# Revit family: PRD_FrankeWS_WlMntdFrntrSpprtRls_BagHolderE-RODX605N,E-RODX607
name_source: partatom
category: Furniture
revit_build: Autodesk Revit 2018 (Build: 20190510_1515(x64)
units: mm (PartAtom-declared; Revit-internal decimal feet)

## family parameters
Cut with Voids When Loaded = No
Host = Face
OmniClass Number = 23.40.20.31.11
OmniClass Title = Bins
Room Calculation Point = No
Shared = No

## types (2) — shared parameters
AssetType = Fixed
BagHolderMaterial = PRD_AR_StainlessSteel_SatinFinished
Category = Pr_40_50_07_96, Waste bins
Color = Stainless steel
Default Elevation = 820 mm
DurationUnit = year
Features = stainless steel, 0.80 mm, satin finished
Finish = Satin finished
FinishAndColour = Stainless steel, satin finished
IfcExportAs = IfcFurnitureType
IfcExportType = NOTDEFINED
IntegralAccessories = includes stainless steel screws and nuts
MainColor = Stainless steel
Manufacturer = KWC Group AG
ManufacturerName = KWC Group AG
ManufacturerURL = www.kwc.com
Material = Stainless steel
Materials = Stainless steel 1.4301
NBSDescription = Bag holder
NBSReference = 45-35-35/450
NominalHeight = 61 mm
ProductInformation = https://pim.kwc.com
Style = Bag holder
TypeOfMounting = Bolt mounting
URL = www.kwc.com
Uniclass2015Code = Pr_20_85_07_97
Uniclass2015Title = Bag holder
Uniclass2015Version = Products v1.10
Version = 1
WarrantyDurationUnit = year

## per-type parameters (varying)
| type | BIMObjectName | Description | GrossWeight | ModelNumber | Name | NetWeight | NominalDepth | NominalWidth | OverallDepth | OverallLength | Size |
| E-RODX605N | PRD_AR_WallMountedFurnitureSupportRails_BagHolderE-RODX605N | Bag holder for waste bin RODX605, RODX605E, RODX605EE, RODX602, RODX602E, RODX617, RODX617E for screwing, stainless steel, surface satin finished, material thickness 0.8 mm / 6 mm, hinged, incl. stainless steel screws and nuts | 0.50 kg | 2030022424 | Bag Holder E-RODX605N | 0.23 kg | 138 mm  [stored 0.452756 ft] | 313 mm  [stored 1.0269 ft] | 138 mm  [stored 0.452756 ft] | 313 mm  [stored 1.0269 ft] | 138x61x313 mm |
| E-RODX607 | PRD_AR_WallMountedFurnitureSupportRails_BagHolderE-RODX607 | Bag holder for waste bin RODX607, for screwing, stainless steel, surface satin finished, material thickness 0.8 mm / 6 mm, hinged, incl. stainless steel screws and nuts. | 0.40 kg | 2000101350 | Bag Holder E-RODX607 | 0.24 kg | 171 mm | 441 mm | 171 mm | 441 mm | 171x61x441 mm |

note: column(s) folded — value = type name in every type: Model, ModelReference

note: [stored X ft] marks values corroborated as IEEE doubles in the binary element streams (Revit-internal decimal feet)

## geometry (parser evidence)
native form markers: Sweep x2
no freeform markers — native parametric forms only
